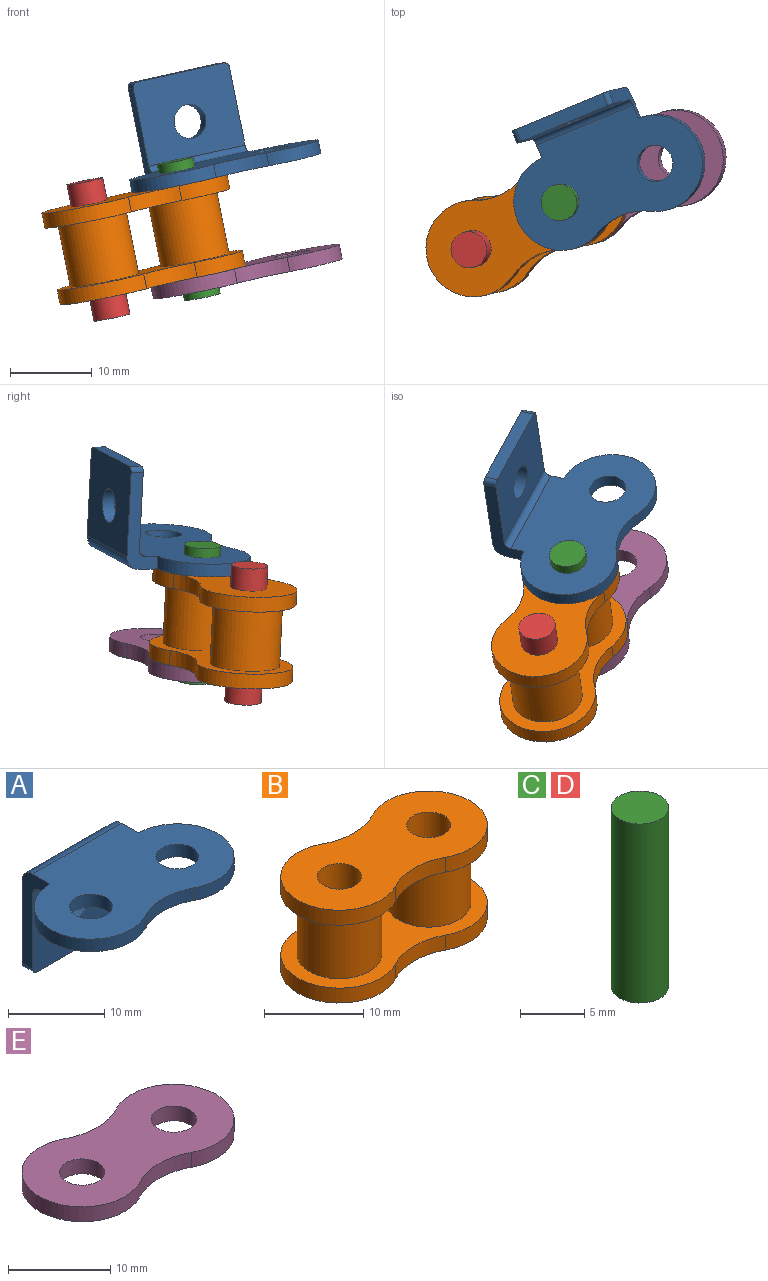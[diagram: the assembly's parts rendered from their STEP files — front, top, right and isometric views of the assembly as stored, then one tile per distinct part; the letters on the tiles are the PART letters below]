
ASSEMBLY  parts=5 mates=4
PART A: 17 faces, bbox 24.5x15.9x12.8 mm
  f0: cylinder r=2.23mm len=4.45mm, axis (0,0,1), area 22.4mm2, adj f8,f9
  f1: cylinder r=2.23mm len=4.45mm, axis (0,0,1), area 22.4mm2, adj f8,f9
  f2: cylinder r=0.8mm len=13mm, axis (1,0,0), area 16.3mm2, adj f3,f4,f9,f13
  f3: plane 12.14x4.1mm, normal (-1,0,0), area 23mm2, adj f2,f4,f5,f7,f8,f9,f10,f15
  f4: plane 13x10.39mm, normal (0,-1,0), area 121mm2, adj f2,f3,f6,f13,f14,f15,f16
  f5: plane 13x11.19mm, normal (0,1,0), area 131.4mm2, adj f3,f6,f7,f13,f14,f15,f16
  f6: plane 11.7x1.6mm, normal (0,0,-1), area 18.7mm2, adj f4,f5,f14,f15
  f7: cylinder r=1.6mm len=13mm, axis (1,0,0), area 32.7mm2, adj f3,f5,f8,f13
  f8: plane 24.5x14.3mm, normal (0,0,1), area 250mm2, adj f0,f1,f3,f7,f10,f11,f12,f13
  f9: plane 24.5x13.5mm, normal (0,0,-1), area 239.6mm2, adj f0,f1,f2,f3,f10,f11,f12,f13
  f10: cylinder r=5.9mm len=11.8mm, axis (0,0,1), area 34.1mm2, adj f3,f8,f9,f11
  f11: cylinder r=7.49mm len=7.11mm, axis (0,0,1), area 11.8mm2, adj f8,f9,f10,f12
  f12: cylinder r=5.9mm len=11.8mm, axis (0,0,1), area 34.1mm2, adj f8,f9,f11,f13
  f13: plane 12.14x4.1mm, normal (1,0,0), area 23mm2, adj f2,f4,f5,f7,f8,f9,f12,f14
  f14: cylinder r=0.65mm len=1.6mm, axis (0,-1,0), area 1.6mm2, adj f4,f5,f6,f13
  f15: cylinder r=0.65mm len=1.6mm, axis (0,-1,0), area 1.6mm2, adj f3,f4,f5,f6
  f16: cylinder r=2.1mm len=4.2mm, axis (0,1,0), area 21.1mm2, adj f4,f5
PART B: 16 faces, bbox 24.5x11.8x11.4 mm
  f0: plane 24.5x11.8mm, normal (0,0,-1), area 124.3mm2, adj f2,f3,f4,f5,f6,f8
  f1: plane 24.5x11.8mm, normal (0,0,1), area 206.9mm2, adj f2,f3,f4,f5,f14,f15
  f2: cylinder r=5.9mm len=11.8mm, axis (0,0,-1), area 44.8mm2, adj f0,f1,f3,f5
  f3: cylinder r=7.49mm len=7.11mm, axis (0,0,-1), area 13.6mm2, adj f0,f1,f2,f4
  f4: cylinder r=5.9mm len=11.8mm, axis (0,0,-1), area 44.8mm2, adj f0,f1,f3,f5
  f5: cylinder r=7.49mm len=7.11mm, axis (0,0,-1), area 13.6mm2, adj f0,f1,f2,f4
  f6: cylinder r=4.25mm len=8.51mm, axis (0,0,1), area 207.2mm2, adj f0,f13
  f7: plane 24.5x11.8mm, normal (0,0,-1), area 206.9mm2, adj f9,f10,f11,f12,f14,f15
  f8: cylinder r=4.25mm len=8.51mm, axis (0,0,1), area 207.2mm2, adj f0,f13
  f9: cylinder r=7.49mm len=7.11mm, axis (0,0,1), area 13.6mm2, adj f7,f10,f12,f13
  f10: cylinder r=5.9mm len=11.8mm, axis (0,0,1), area 44.8mm2, adj f7,f9,f11,f13
  f11: cylinder r=7.49mm len=7.11mm, axis (0,0,1), area 13.6mm2, adj f7,f10,f12,f13
  f12: cylinder r=5.9mm len=11.8mm, axis (0,0,1), area 44.8mm2, adj f7,f9,f11,f13
  f13: plane 24.5x11.8mm, normal (0,0,1), area 124.3mm2, adj f6,f8,f9,f10,f11,f12
  f14: cylinder r=2.23mm len=11.43mm, axis (0,0,1), area 159.8mm2, adj f1,f7
  f15: cylinder r=2.23mm len=11.43mm, axis (0,0,1), area 159.8mm2, adj f1,f7
PART C: 3 faces, bbox 4.5x4.5x17 mm
  f0: cylinder r=2.23mm len=17mm, axis (0,0,1), area 237.7mm2, adj f1,f2
  f1: plane 4.45x4.45mm, normal (0,0,-1), area 15.6mm2, adj f0
  f2: plane 4.45x4.45mm, normal (0,0,1), area 15.6mm2, adj f0
PART D: same geometry as C
PART E: 8 faces, bbox 24.5x11.8x1.8 mm
  f0: plane 24.5x11.8mm, normal (0,0,1), area 206.9mm2, adj f1,f3,f4,f5,f6,f7
  f1: cylinder r=2.23mm len=4.45mm, axis (0,0,1), area 24.8mm2, adj f0,f2
  f2: plane 24.5x11.8mm, normal (0,0,-1), area 206.9mm2, adj f1,f3,f4,f5,f6,f7
  f3: cylinder r=7.49mm len=7.11mm, axis (0,0,1), area 13.1mm2, adj f0,f2,f4,f6
  f4: cylinder r=5.9mm len=11.8mm, axis (0,0,1), area 43.2mm2, adj f0,f2,f3,f5
  f5: cylinder r=7.49mm len=7.11mm, axis (0,0,1), area 13.1mm2, adj f0,f2,f4,f6
  f6: cylinder r=5.9mm len=11.8mm, axis (0,0,1), area 43.2mm2, adj f0,f2,f3,f5
  f7: cylinder r=2.23mm len=4.45mm, axis (0,0,1), area 24.8mm2, adj f0,f2
PLACE A rot(axis=(-0.19,0.98,0.01),168.4deg) t=(-39.6,24.42,-52.52)mm
PLACE B rot(axis=(-0.97,-0.23,-0.1),179.9deg) t=(-60.71,14.28,-64.72)mm
PLACE C rot(axis=(0.13,-0.12,-0.98),68.6deg) t=(-49.67,20.03,-62.22)mm
PLACE D rot(axis=(0,-0.4,0.92),29.6deg) t=(-60.71,14.28,-64.72)mm
PLACE E rot(axis=(0.02,-0.47,0.88),25.1deg) t=(-48.2,20.4,-69.56)mm
MATE fastened D.f0 <-> B.f6  axis (-0.2,-0.05,0.98) through (-60.71,14.28,-64.72)mm
MATE revolute C.f0 <-> B.f8  axis (-0.2,-0.05,0.98) through (-49.67,20.03,-62.22)mm
MATE fastened A.f1 <-> C.f0  axis (0.2,0.05,-0.98) through (-50.79,19.75,-56.63)mm
MATE fastened E.f1 <-> C.f0  axis (-0.2,-0.05,0.98) through (-48.55,20.31,-67.82)mm
